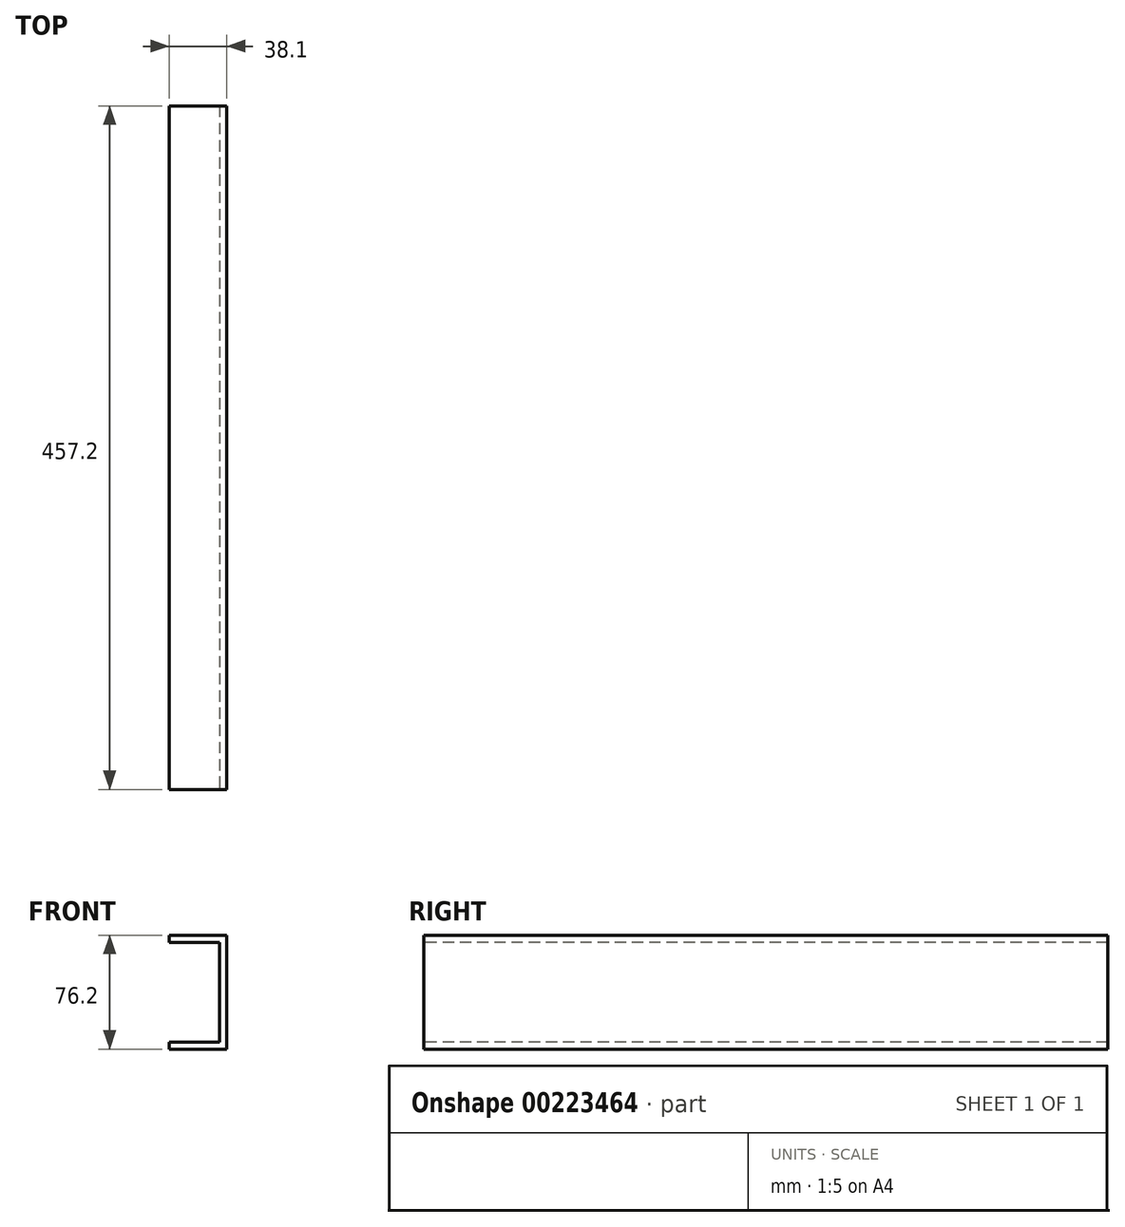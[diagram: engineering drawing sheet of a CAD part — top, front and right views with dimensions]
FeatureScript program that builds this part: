
annotation { "Feature Type Name" : "Feature", "Feature Type Description" : "" }
export const myFeature = defineFeature(function(context is Context, id is Id, definition is map)
    precondition{}
    {
        {
            var Q0;
            Q0=qCreatedBy(makeId("Right.planeOp"),FACE);
            var sketch = newSketch(context, id + "F0", { "sketchPlane" : qUnion([Q0])});
            skLineSegment(sketch, "E0.bottom", {"start": v(298.75, -35.06) * mm, "end": v(-158.45, -35.06) * mm});
            skLineSegment(sketch, "E0.top", {"start": v(298.75, 41.14) * mm, "end": v(-158.45, 41.14) * mm});
            skLineSegment(sketch, "E0.left", {"start": v(298.75, -35.06) * mm, "end": v(298.75, 41.14) * mm});
            skLineSegment(sketch, "E0.right", {"start": v(-158.45, -35.06) * mm, "end": v(-158.45, 41.14) * mm});
            skSolve(sketch);
        }
        {
            var Q0;
            Q0 = qSketchRegion(id + "F0", true);
            extrude(context, id + "F1", {"entities" : qUnion([Q0]), "oppositeDirection" : true, "depth" : 38.1 * mm});
        }
        {
            var Q0;
            Q0=makeQuery(id+"F1.opExtrude","SWEPT_FACE",FACE,{"disambiguationData":[OSD([sQuery(id+"F0.wireOp",EDGE,"E0.right")])]});
            var sketch = newSketch(context, id + "F2", { "sketchPlane" : qUnion([Q0])});
            skLineSegment(sketch, "E1.bottom", {"start": v(-38.1, -30.3) * mm, "end": v(-4.76, -30.3) * mm});
            skLineSegment(sketch, "E1.top", {"start": v(-38.1, 36.37) * mm, "end": v(-4.76, 36.37) * mm});
            skLineSegment(sketch, "E1.left", {"start": v(-38.1, -30.3) * mm, "end": v(-38.1, 36.37) * mm});
            skLineSegment(sketch, "E1.right", {"start": v(-4.76, -30.3) * mm, "end": v(-4.76, 36.37) * mm});
            skSolve(sketch);
        }
        {
            var Q0;
            Q0 = qSketchRegion(id + "F2", true);
            extrude(context, id + "F3", {"entities" : qUnion([Q0]), "operationType" : NewBodyOperationType.REMOVE, "oppositeDirection" : true, "depth" : 482.6 * mm});
        }
    });
